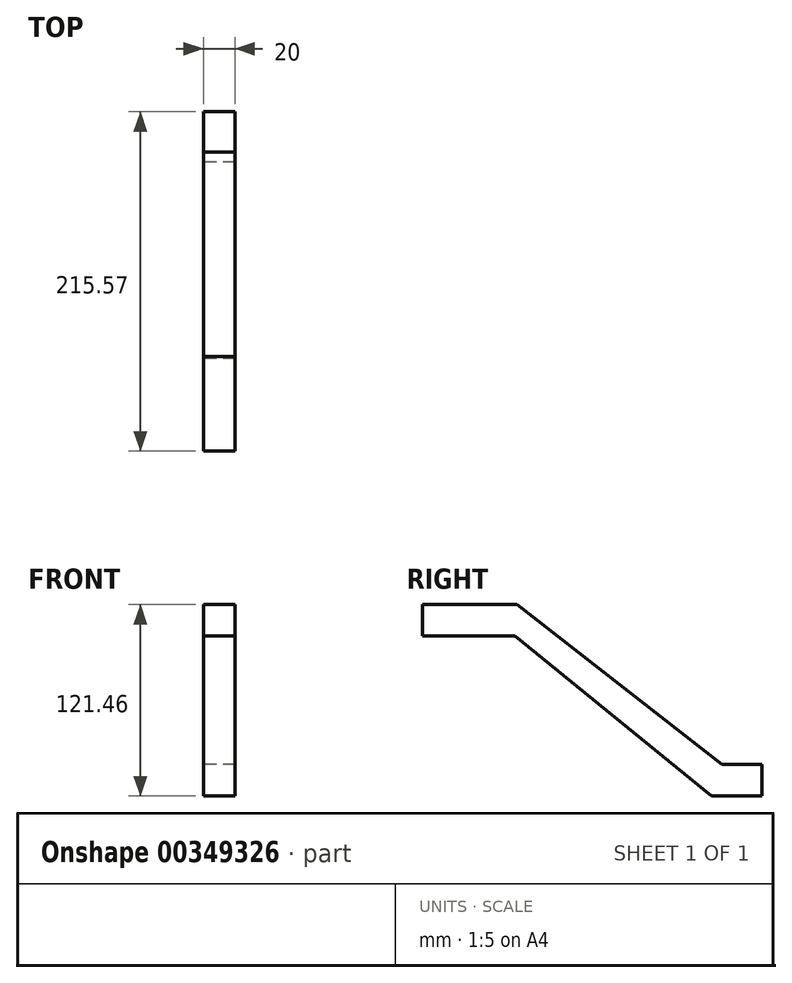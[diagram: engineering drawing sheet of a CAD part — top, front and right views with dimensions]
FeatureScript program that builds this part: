
annotation { "Feature Type Name" : "Feature", "Feature Type Description" : "" }
export const myFeature = defineFeature(function(context is Context, id is Id, definition is map)
    precondition{}
    {
        {
            var Q0;
            Q0=qCreatedBy(makeId("Right.planeOp"),FACE);
            var sketch = newSketch(context, id + "F0", { "sketchPlane" : qUnion([Q0])});
            skPoint(sketch, "E0.middle", {"position": v(0, 0) * mm});
            skLineSegment(sketch, "E1", {"start": v(-77.79, 60.73) * mm, "end": v(-87.65, 60.73) * mm});
            skLineSegment(sketch, "E2", {"start": v(-87.65, 60.73) * mm, "end": v(-61.75, 60.73) * mm});
            skLineSegment(sketch, "E3", {"start": v(61.75, -60.73) * mm, "end": v(87.65, -60.73) * mm});
            skLineSegment(sketch, "E4", {"start": v(83.86, -52.95) * mm, "end": v(93.82, -60.73) * mm});
            skLineSegment(sketch, "E5", {"start": v(93.82, -60.73) * mm, "end": v(87.65, -60.73) * mm});
            skLineSegment(sketch, "E6", {"start": v(-87.65, 60.73) * mm, "end": v(61.75, -60.73) * mm});
            skLineSegment(sketch, "E7", {"start": v(93.82, -60.73) * mm, "end": v(93.82, -40.73) * mm});
            skLineSegment(sketch, "E8", {"start": v(93.82, -40.73) * mm, "end": v(68.2, -40.73) * mm});
            skLineSegment(sketch, "E9", {"start": v(-61.75, 60.73) * mm, "end": v(68.2, -40.73) * mm});
            skLineSegment(sketch, "E10", {"start": v(-61.75, 60.73) * mm, "end": v(-61.75, 40.73) * mm});
            skLineSegment(sketch, "E11", {"start": v(-61.75, 40.73) * mm, "end": v(-121.75, 40.73) * mm});
            skLineSegment(sketch, "E12", {"start": v(-121.75, 40.73) * mm, "end": v(-121.75, 60.73) * mm});
            skLineSegment(sketch, "E13", {"start": v(-121.75, 60.73) * mm, "end": v(-87.65, 60.73) * mm});
            skLineSegment(sketch, "E14", {"start": v(61.75, -60.73) * mm, "end": v(-121.75, -60.73) * mm});
            skSolve(sketch);
        }
        {
            var Q0;
            Q0 = qSketchRegion(id + "F0", true);
            extrude(context, id + "F1", {"entities" : qUnion([Q0]), "endBound" : BoundingType.SYMMETRIC, "depth" : 20 * mm});
        }
    });
